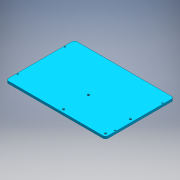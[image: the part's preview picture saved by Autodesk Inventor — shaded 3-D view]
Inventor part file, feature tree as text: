
AUTODESK INVENTOR PART (.ipt)
format: ipt  version: 2016 (Build 200138000, 138)  size: 133,120 bytes
history: native  units: mm
features: sketch x3, hole x2, extrude x1
ambient origin geometry x8: Origin, YZ Plane, XZ Plane, XY Plane, X Axis, Y Axis, Z Axis, Center Point
bodies: Solid1 (feature_tree)
feature tree (6):
  extrude  "Extrusion1"  Depth=110.0mm
  hole  "Hole1"  [1 undecoded]
  hole  "Hole2"  [1 undecoded]
  sketch  "Sketch1"  dims[d0=160.0mm d1=110.0mm]
  sketch  "Sketch2"  dims[d2=55.0mm d3=80.0mm]
  sketch  "Sketch3"  dims[d4=4.0mm d5=3.75mm d6=0.0mm d7=156.6mm d8=76.0mm d9=38.0mm d10=78.3mm d11=2.013mm d12=5.0mm d13=11.0mm d14=2.6mm d15=14.3117mm d16=7.6mm d17=20.594885mm d18=40.0mm d19=67.5mm d20=5.0mm d21=5.0mm d22=3.242mm d23=8.0mm d24=11.0mm d25=2.6mm d26=14.3117mm d27=11.8mm d28=20.594885mm]
note: 2 required parameter values undecoded (feature->parameter linkage not recoverable at this tier; creation-order binding heuristic only, values carry confidence <= 0.55)
